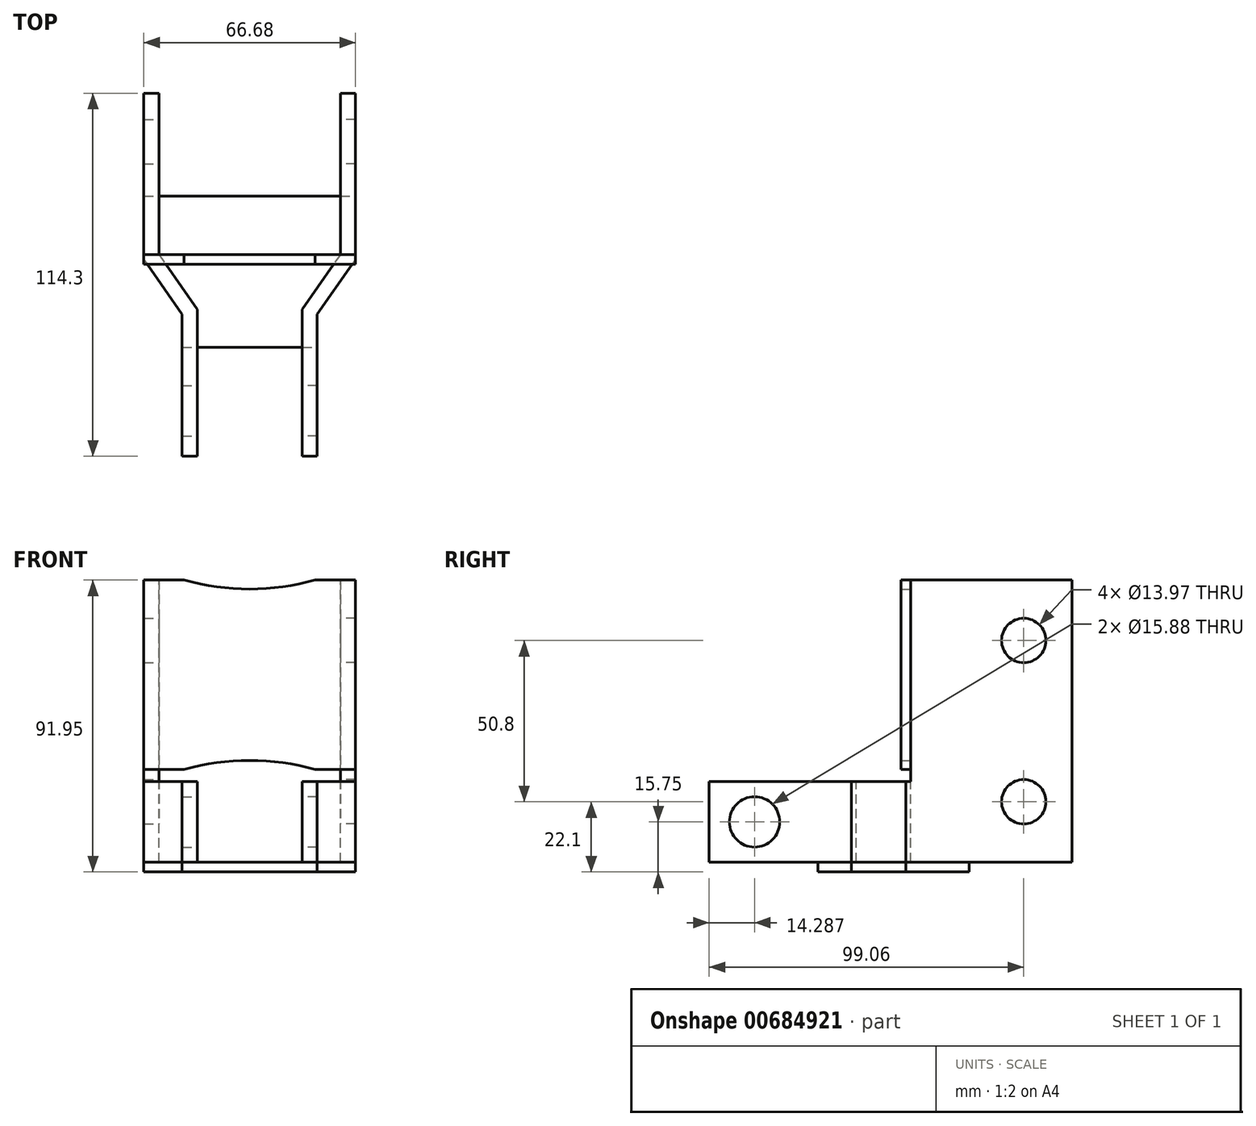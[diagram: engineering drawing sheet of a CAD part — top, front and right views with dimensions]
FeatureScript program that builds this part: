
annotation { "Feature Type Name" : "Feature", "Feature Type Description" : "" }
export const myFeature = defineFeature(function(context is Context, id is Id, definition is map)
    precondition{}
    {
        {
            var Q0;
            Q0=qCreatedBy(makeId("Top.planeOp"),FACE);
            var sketch = newSketch(context, id + "F0", { "sketchPlane" : qUnion([Q0])});
            skLineSegment(sketch, "E0", {"start": v(0, 36.1) * mm, "end": v(0, -89.76) * mm, "construction": true});
            skLineSegment(sketch, "E1", {"start": v(28.58, 0) * mm, "end": v(28.58, -50.8) * mm});
            skLineSegment(sketch, "E2", {"start": v(28.58, -50.8) * mm, "end": v(16.51, -68.03) * mm});
            skLineSegment(sketch, "E3", {"start": v(16.51, -68.03) * mm, "end": v(16.51, -114.3) * mm});
            skLineSegment(sketch, "E4.0", {"start": v(21.27, -69.53) * mm, "end": v(21.27, -114.3) * mm});
            skLineSegment(sketch, "E5.0", {"start": v(33.34, -52.3) * mm, "end": v(21.27, -69.53) * mm});
            skLineSegment(sketch, "E5.1", {"start": v(33.34, 0) * mm, "end": v(33.34, -52.3) * mm});
            skLineSegment(sketch, "E6", {"start": v(16.51, -114.3) * mm, "end": v(21.27, -114.3) * mm});
            skLineSegment(sketch, "E7", {"start": v(28.58, 0) * mm, "end": v(33.34, 0) * mm});
            skSolve(sketch);
        }
        {
            var Q0;
            Q0 = qSketchRegion(id + "F0", true);
            extrude(context, id + "F1", {"entities" : qUnion([Q0]), "oppositeDirection" : true, "depth" : 88.9 * mm, "offsetDistance" : 25.4 * mm});
        }
        {
            var Q0;
            Q0=qCreatedBy(makeId("Right.planeOp"),FACE);
            var sketch = newSketch(context, id + "F2", { "sketchPlane" : qUnion([Q0])});
            skLineSegment(sketch, "E8", {"start": v(-15.24, 19.21) * mm, "end": v(-15.24, -142.93) * mm, "construction": true});
            skLineSegment(sketch, "E9", {"start": v(0, -44.45) * mm, "end": v(-158.44, -44.45) * mm, "construction": true});
            skLineSegment(sketch, "E10", {"start": v(-50.8, 0) * mm, "end": v(-50.8, -63.5) * mm});
            skLineSegment(sketch, "E11", {"start": v(-50.8, -63.5) * mm, "end": v(-114.3, -63.5) * mm});
            skLineSegment(sketch, "E12", {"start": v(-114.3, -63.5) * mm, "end": v(-114.3, 0) * mm});
            skLineSegment(sketch, "E13", {"start": v(-114.3, 0) * mm, "end": v(-50.8, 0) * mm});
            skCircle(sketch, "E14", {"center": v(-15.24, -19.05) * mm, "radius": 6.99 * mm});
            skCircle(sketch, "E15.MirrorC", {"center": v(-15.24, -69.85) * mm, "radius": 6.99 * mm});
            skCircle(sketch, "E16", {"center": v(-100.01, -76.2) * mm, "radius": 7.94 * mm});
            skLineSegment(sketch, "E17", {"start": v(-100.01, -63.5) * mm, "end": v(-100.01, -88.9) * mm, "construction": true});
            skLineSegment(sketch, "E18", {"start": v(-100.01, -76.2) * mm, "end": v(-92.43, -76.2) * mm, "construction": true});
            skSolve(sketch);
        }
        {
            var Q0;
            Q0=qSketchRegion(id+"F2",true);
            extrude(context, id + "F3", {"entities" : qUnion([Q0]), "operationType" : NewBodyOperationType.REMOVE, "endBound" : BoundingType.THROUGH_ALL, "depth" : 27.64 * mm, "offsetDistance" : 25.4 * mm});
        }
        {
            var Q0;
            Q0=makeQuery(id+"F1.opExtrude","SWEPT_BODY",BODY,{"disambiguationData":[OSD([sQuery(id+"F0.wireOp",EDGE,"E1"),sQuery(id+"F0.wireOp",EDGE,"E2"),sQuery(id+"F0.wireOp",EDGE,"E3"),sQuery(id+"F0.wireOp",EDGE,"E4.0"),sQuery(id+"F0.wireOp",EDGE,"E5.0"),sQuery(id+"F0.wireOp",EDGE,"E5.1"),sQuery(id+"F0.wireOp",EDGE,"E6"),sQuery(id+"F0.wireOp",EDGE,"E7")])]});
            var Q1;
            Q1=qCreatedBy(makeId("Right.planeOp"),FACE);
            mirror(context, id + "F4", {"entities" : qUnion([Q0]), "mirrorPlane" : qUnion([Q1])});
        }
        {
            var Q0;
            Q0=makeQuery(id+"F4.opPattern","COPY",FACE,{"derivedFrom":makeQuery(id+"F3.boolean.opBoolean","COPY",FACE,{"derivedFrom":makeQuery(id+"F3.opExtrude","SWEPT_FACE",FACE,{"disambiguationData":[OSD([sQuery(id+"F2.wireOp",EDGE,"E10")])]})}),"instanceName":"1"});
            var sketch = newSketch(context, id + "F5", { "sketchPlane" : qUnion([Q0])});
            skLineSegment(sketch, "E19.bottom", {"start": v(-33.34, 0) * mm, "end": v(-20.64, 0) * mm});
            skLineSegment(sketch, "E19.top", {"start": v(-33.34, -59.69) * mm, "end": v(-20.64, -59.69) * mm});
            skLineSegment(sketch, "E19.left", {"start": v(-33.34, 0) * mm, "end": v(-33.34, -59.69) * mm});
            skLineSegment(sketch, "E19.right", {"start": v(33.34, 0) * mm, "end": v(33.34, -59.69) * mm});
            skLineSegment(sketch, "E20", {"start": v(0, 7.08) * mm, "end": v(0, -133.04) * mm, "construction": true});
            skArc(sketch, "E21", {"start": v(-20.64, -59.69) * mm, "mid": v(0, -56.84) * mm, "end": v(20.64, -59.69) * mm});
            skLineSegment(sketch, "E22.trimOffspring", {"start": v(20.64, -59.69) * mm, "end": v(33.34, -59.69) * mm});
            skLineSegment(sketch, "E23", {"start": v(-33.34, -29.85) * mm, "end": v(33.34, -29.85) * mm, "construction": true});
            skPoint(sketch, "E23.startSnap0", {"position": v(-33.34, -29.84) * mm});
            skArc(sketch, "E24.MirrorCS", {"start": v(-20.64, 0) * mm, "mid": v(0, -2.85) * mm, "end": v(20.64, 0) * mm});
            skLineSegment(sketch, "E25.trimOffspring", {"start": v(20.64, 0) * mm, "end": v(33.34, 0) * mm});
            skSolve(sketch);
        }
        {
            var Q0;
            Q0 = qSketchRegion(id + "F5", true);
            extrude(context, id + "F6", {"entities" : qUnion([Q0]), "depth" : 3.05 * mm, "offsetDistance" : 25.4 * mm});
        }
        {
            var Q0;
            Q0=makeQuery(id+"F4.opPattern","COPY",FACE,{"derivedFrom":makeQuery(id+"F1.opExtrude","CAP_FACE",FACE,{"disambiguationData":[OSD([sQuery(id+"F0.wireOp",EDGE,"E1"),sQuery(id+"F0.wireOp",EDGE,"E2"),sQuery(id+"F0.wireOp",EDGE,"E3"),sQuery(id+"F0.wireOp",EDGE,"E4.0"),sQuery(id+"F0.wireOp",EDGE,"E5.0"),sQuery(id+"F0.wireOp",EDGE,"E5.1"),sQuery(id+"F0.wireOp",EDGE,"E6"),sQuery(id+"F0.wireOp",EDGE,"E7")])],"isStart":false}),"instanceName":"1"});
            var sketch = newSketch(context, id + "F7", { "sketchPlane" : qUnion([Q0])});
            skLineSegment(sketch, "E26", {"start": v(-33.34, 32.39) * mm, "end": v(-33.34, 52.3) * mm});
            skLineSegment(sketch, "E27", {"start": v(-33.34, 52.3) * mm, "end": v(-21.27, 69.53) * mm});
            skLineSegment(sketch, "E28", {"start": v(21.27, 69.53) * mm, "end": v(33.34, 52.3) * mm});
            skLineSegment(sketch, "E29", {"start": v(33.34, 52.3) * mm, "end": v(33.34, 32.39) * mm});
            skLineSegment(sketch, "E30", {"start": v(-33.34, 32.39) * mm, "end": v(33.34, 32.39) * mm});
            skLineSegment(sketch, "E31", {"start": v(-21.27, 69.53) * mm, "end": v(-21.27, 80.01) * mm});
            skLineSegment(sketch, "E32", {"start": v(-21.27, 80.01) * mm, "end": v(21.27, 80.01) * mm});
            skLineSegment(sketch, "E33", {"start": v(21.27, 80.01) * mm, "end": v(21.27, 69.53) * mm});
            skSolve(sketch);
        }
        {
            var Q0;
            Q0 = qSketchRegion(id + "F7", true);
            extrude(context, id + "F8", {"entities" : qUnion([Q0]), "depth" : 3.05 * mm, "offsetDistance" : 25.4 * mm});
        }
    });
